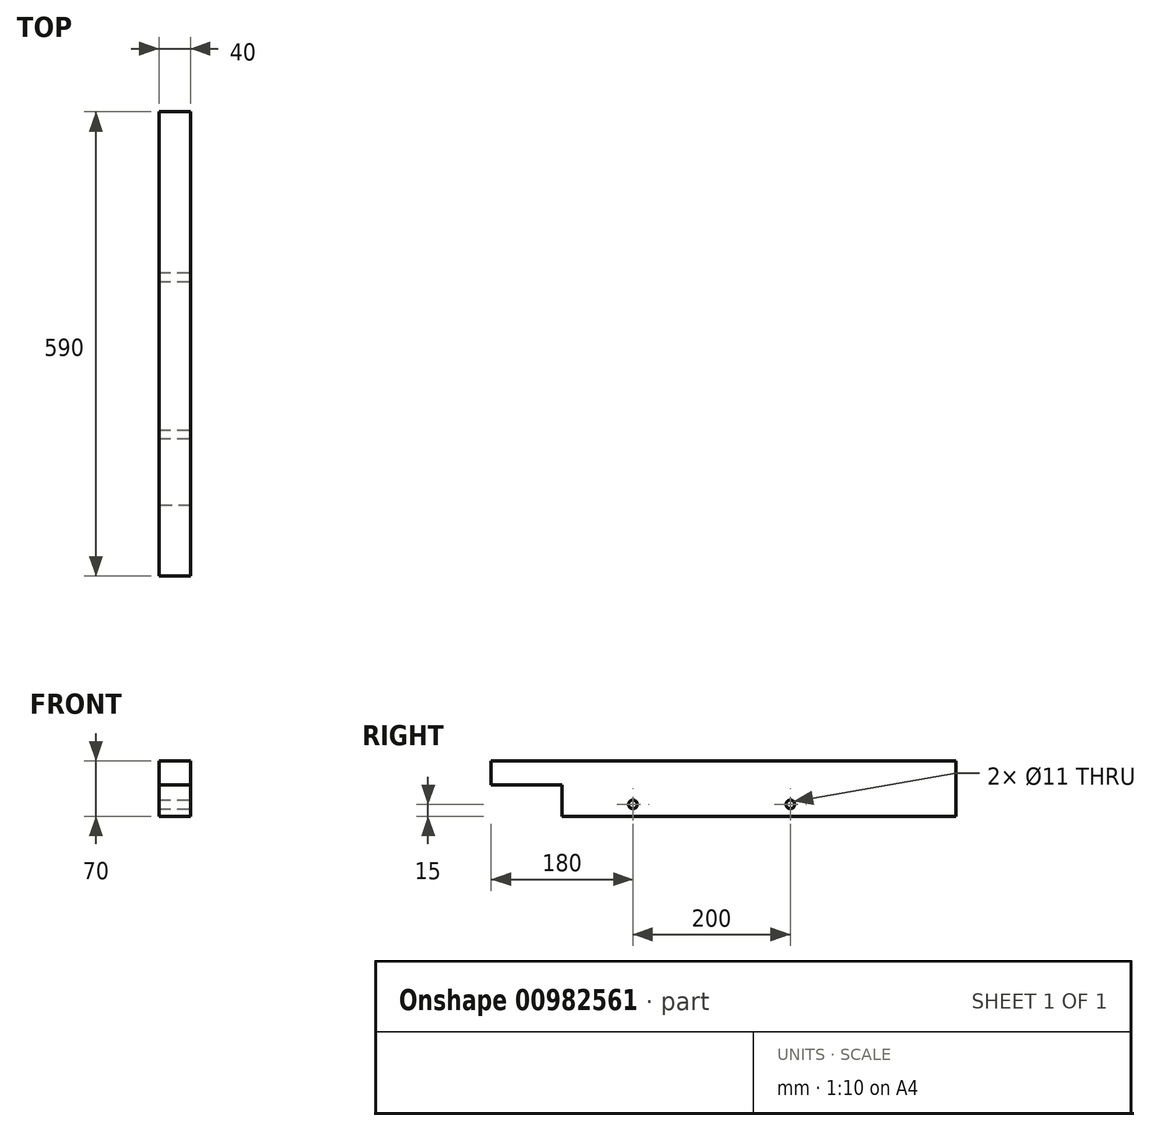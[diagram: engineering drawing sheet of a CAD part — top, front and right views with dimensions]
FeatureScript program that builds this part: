
annotation { "Feature Type Name" : "Feature", "Feature Type Description" : "" }
export const myFeature = defineFeature(function(context is Context, id is Id, definition is map)
    precondition{}
    {
        {
            var Q0;
            Q0=qCreatedBy(makeId("Front.planeOp"),FACE);
            var sketch = newSketch(context, id + "F0", { "sketchPlane" : qUnion([Q0])});
            skLineSegment(sketch, "E0", {"start": v(0, 0) * mm, "end": v(0, 70) * mm});
            skLineSegment(sketch, "E1", {"start": v(0, 70) * mm, "end": v(40, 70) * mm});
            skLineSegment(sketch, "E2", {"start": v(40, 70) * mm, "end": v(40, 0) * mm});
            skLineSegment(sketch, "E3", {"start": v(40, 0) * mm, "end": v(0, 0) * mm});
            skSolve(sketch);
        }
        {
            var Q0;
            Q0=makeQuery(id+"F0.imprint","IMPRINT",FACE,{"disambiguationData":[TD([[makeQuery(id+"F0.imprint","IMPRINT",EDGE,{"derivedFrom":sQuery(id+"F0.wireOp",EDGE,"E0")}),-1.0]])]});
            extrude(context, id + "F1", {"entities" : qUnion([Q0]), "depth" : 500 * mm, "offsetDistance" : 25 * mm});
        }
        {
            var Q0;
            Q0=makeQuery(id+"F1.opExtrude","SWEPT_FACE",FACE,{"disambiguationData":[OSD([sQuery(id+"F0.wireOp",EDGE,"E2")])]});
            var sketch = newSketch(context, id + "F2", { "sketchPlane" : qUnion([Q0])});
            skPoint(sketch, "E4", {"position": v(-410, 15) * mm});
            skPoint(sketch, "E5", {"position": v(-210, 15) * mm});
            skSolve(sketch);
        }
        {
            var Q0;
            Q0=sQuery(id+"F2.wireOp",VERTEX,"E4");
            var Q1;
            Q1=sQuery(id+"F2.wireOp",VERTEX,"E5");
            var Q2;
            Q2=makeQuery(id+"F1.opExtrude","SWEPT_BODY",BODY,{"disambiguationData":[OSD([sQuery(id+"F0.wireOp",EDGE,"E0"),sQuery(id+"F0.wireOp",EDGE,"E1"),sQuery(id+"F0.wireOp",EDGE,"E2"),sQuery(id+"F0.wireOp",EDGE,"E3")])]});
            hole(context, id + "F3", {"style" : HoleStyle.SIMPLE, "endStyle" : HoleEndStyle.BLIND, "holeDiameter" : 11 * mm, "majorDiameter" : 5 * mm, "holeDepth" : 50 * mm, "isTappedThrough" : true, "tappedDepth" : 4 * mm, "tapClearance" : 3, "startFromSketch" : true, "locations" : qUnion([Q0, Q1]), "scope" : qUnion([Q2])});
        }
        {
            var Q0;
            Q0=makeQuery(id+"F1.opExtrude","CAP_FACE",FACE,{"disambiguationData":[OSD([sQuery(id+"F0.wireOp",EDGE,"E0"),sQuery(id+"F0.wireOp",EDGE,"E1"),sQuery(id+"F0.wireOp",EDGE,"E2"),sQuery(id+"F0.wireOp",EDGE,"E3")])],"isStart":false});
            var sketch = newSketch(context, id + "F4", { "sketchPlane" : qUnion([Q0])});
            skLineSegment(sketch, "E6.bottom", {"start": v(0, 70) * mm, "end": v(40, 70) * mm});
            skLineSegment(sketch, "E6.top", {"start": v(0, 40) * mm, "end": v(40, 40) * mm});
            skLineSegment(sketch, "E6.left", {"start": v(0, 70) * mm, "end": v(0, 40) * mm});
            skLineSegment(sketch, "E6.right", {"start": v(40, 70) * mm, "end": v(40, 40) * mm});
            skSolve(sketch);
        }
        {
            var Q0;
            Q0=qSketchRegion(id+"F4",true);
            extrude(context, id + "F5", {"entities" : qUnion([Q0]), "operationType" : NewBodyOperationType.ADD, "depth" : 90 * mm, "offsetDistance" : 25 * mm});
        }
    });
